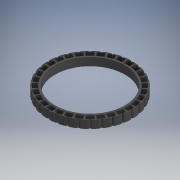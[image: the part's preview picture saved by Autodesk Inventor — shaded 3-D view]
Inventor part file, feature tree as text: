
AUTODESK INVENTOR PART (.ipt)
format: ipt  version: 2020 (Build 240168000, 168)  size: 730,624 bytes
history: native  units: mm
features: extrude x3, sketch x2, other x1
ambient origin geometry x8: Origin, YZ Plane, XZ Plane, XY Plane, X Axis, Y Axis, Z Axis, Center Point
bodies: Body1 (feature_tree)
feature tree (6):
  other  "tsop_lid"
  sketch  "Эскиз1"
  sketch  "Эскиз3"
  extrude  "Выдавливание4"  Depth=7.2mm
  extrude  "Выдавливание3"  Depth=5.2mm
  extrude  "Выдавливание5"  Depth=320.0mm TaperAngle=360.0deg
